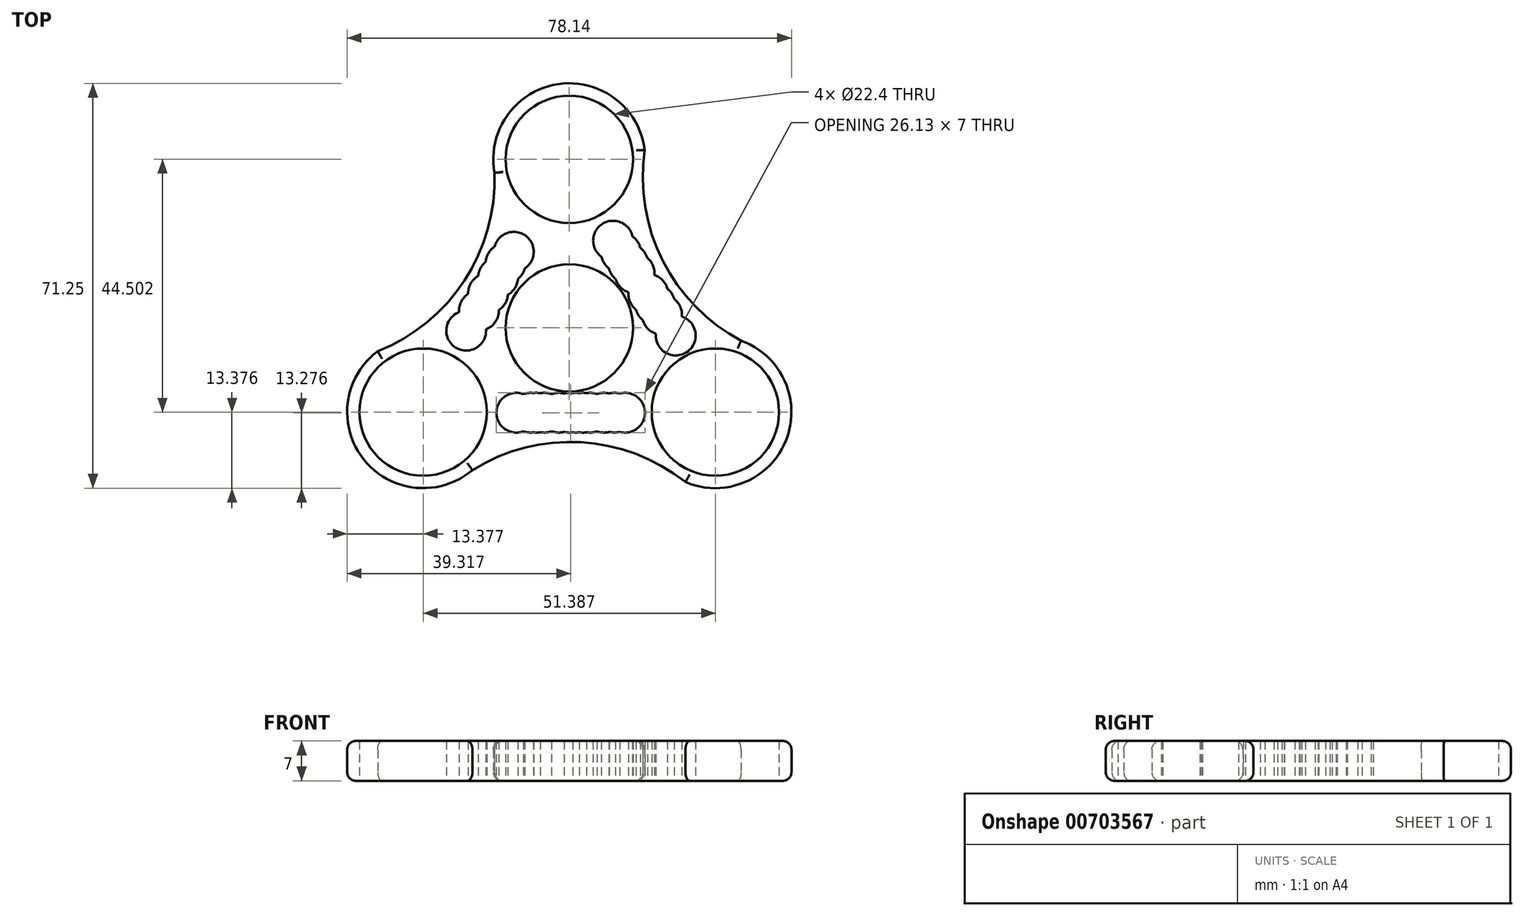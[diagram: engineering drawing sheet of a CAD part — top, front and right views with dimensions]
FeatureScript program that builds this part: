
annotation { "Feature Type Name" : "Feature", "Feature Type Description" : "" }
export const myFeature = defineFeature(function(context is Context, id is Id, definition is map)
    precondition{}
    {
        {
            var Q0;
            Q0=qCreatedBy(makeId("Top.planeOp"),FACE);
            var sketch = newSketch(context, id + "F0", { "sketchPlane" : qUnion([Q0])});
            skCircle(sketch, "E0", {"center": v(0, 0) * mm, "radius": 11.2 * mm});
            skCircle(sketch, "E1", {"center": v(0, 29.67) * mm, "radius": 11.2 * mm});
            skArc(sketch, "E2", {"start": v(12.93, 26.26) * mm, "mid": v(0.52, 43.03) * mm, "end": v(-13.16, 27.28) * mm});
            skArc(sketch, "E3.1.0", {"start": v(-29.21, -1.93) * mm, "mid": v(-37.53, -21.07) * mm, "end": v(-17.04, -25.03) * mm});
            skCircle(sketch, "E3.1.1", {"center": v(-25.7, -14.83) * mm, "radius": 11.2 * mm});
            skArc(sketch, "E3.2.0", {"start": v(16.28, -24.33) * mm, "mid": v(37, -21.97) * mm, "end": v(30.2, -2.24) * mm});
            skCircle(sketch, "E3.2.1", {"center": v(25.7, -14.83) * mm, "radius": 11.2 * mm});
            skArc(sketch, "E4", {"start": v(13.28, 31.24) * mm, "mid": v(16.43, 11.82) * mm, "end": v(30.2, -2.24) * mm});
            skArc(sketch, "E5.1.0", {"start": v(-33.7, -4.12) * mm, "mid": v(-18.45, 8.32) * mm, "end": v(-13.16, 27.28) * mm});
            skArc(sketch, "E5.2.0", {"start": v(20.42, -27.12) * mm, "mid": v(2.02, -20.14) * mm, "end": v(-17.04, -25.03) * mm});
            skSolve(sketch);
        }
        {
            var Q0;
            Q0=makeQuery(id+"F0.imprint","IMPRINT",FACE,{"disambiguationData":[TD([[makeQuery(id+"F0.imprint","IMPRINT",EDGE,{"derivedFrom":sQuery(id+"F0.wireOp",EDGE,"E0")}),-1.0]])]});
            extrude(context, id + "F1", {"entities" : qUnion([Q0]), "depth" : 7 * mm, "offsetDistance" : 25 * mm});
        }
        {
            var Q0;
            Q0=makeQuery(id+"F1.opExtrude","CAP_EDGE",EDGE,{"disambiguationData":[OSD([sQuery(id+"F0.wireOp",EDGE,"E5.1.0")])],"isStart":false});
            var Q1;
            Q1=makeQuery(id+"F1.opExtrude","CAP_EDGE",EDGE,{"disambiguationData":[OSD([sQuery(id+"F0.wireOp",EDGE,"E2")])],"isStart":false});
            var Q2;
            Q2=makeQuery(id+"F1.opExtrude","CAP_EDGE",EDGE,{"disambiguationData":[OSD([sQuery(id+"F0.wireOp",EDGE,"E4")])],"isStart":false});
            var Q3;
            Q3=makeQuery(id+"F1.opExtrude","CAP_EDGE",EDGE,{"disambiguationData":[OSD([sQuery(id+"F0.wireOp",EDGE,"E3.2.0")])],"isStart":false});
            var Q4;
            Q4=makeQuery(id+"F1.opExtrude","CAP_EDGE",EDGE,{"disambiguationData":[OSD([sQuery(id+"F0.wireOp",EDGE,"E5.2.0")])],"isStart":false});
            var Q5;
            Q5=makeQuery(id+"F1.opExtrude","CAP_EDGE",EDGE,{"disambiguationData":[OSD([sQuery(id+"F0.wireOp",EDGE,"E3.1.0")])],"isStart":false});
            fillet(context, id + "F2", {"entities" : qUnion([Q0, Q1, Q2, Q3, Q4, Q5]), "radius" : 1.5 * mm, "tangentPropagation" : true, "allowEdgeOverflow" : false});
        }
        {
            var Q0;
            Q0=makeQuery(id+"F1.opExtrude","CAP_EDGE",EDGE,{"disambiguationData":[OSD([sQuery(id+"F0.wireOp",EDGE,"E3.1.0")])],"isStart":true});
            var Q1;
            Q1=makeQuery(id+"F1.opExtrude","CAP_EDGE",EDGE,{"disambiguationData":[OSD([sQuery(id+"F0.wireOp",EDGE,"E5.2.0")])],"isStart":true});
            var Q2;
            Q2=makeQuery(id+"F1.opExtrude","CAP_EDGE",EDGE,{"disambiguationData":[OSD([sQuery(id+"F0.wireOp",EDGE,"E5.1.0")])],"isStart":true});
            var Q3;
            Q3=makeQuery(id+"F1.opExtrude","CAP_EDGE",EDGE,{"disambiguationData":[OSD([sQuery(id+"F0.wireOp",EDGE,"E2")])],"isStart":true});
            var Q4;
            Q4=makeQuery(id+"F1.opExtrude","CAP_EDGE",EDGE,{"disambiguationData":[OSD([sQuery(id+"F0.wireOp",EDGE,"E3.2.0")])],"isStart":true});
            var Q5;
            Q5=makeQuery(id+"F1.opExtrude","CAP_EDGE",EDGE,{"disambiguationData":[OSD([sQuery(id+"F0.wireOp",EDGE,"E4")])],"isStart":true});
            fillet(context, id + "F3", {"entities" : qUnion([Q0, Q1, Q2, Q3, Q4, Q5]), "radius" : 1.5 * mm, "tangentPropagation" : true, "allowEdgeOverflow" : false});
        }
        {
            var Q0;
            Q0=qCreatedBy(makeId("Top.planeOp"),FACE);
            var sketch = newSketch(context, id + "F4", { "sketchPlane" : qUnion([Q0])});
            skLineSegment(sketch, "E6", {"start": v(-14.58, 6.83) * mm, "end": v(-15.9, 5.37) * mm, "construction": true});
            skLineSegment(sketch, "E7", {"start": v(-15.9, 5.37) * mm, "end": v(-14.58, 6.83) * mm, "construction": true});
            skLineSegment(sketch, "E8", {"start": v(-15.9, 3.03) * mm, "end": v(-15.9, 0) * mm, "construction": true});
            skLineSegment(sketch, "E9", {"start": v(-15.9, 0) * mm, "end": v(-15.9, 3.03) * mm, "construction": true});
            skLineSegment(sketch, "E10", {"start": v(-12.53, 8.87) * mm, "end": v(-11.07, 10.92) * mm, "construction": true});
            skLineSegment(sketch, "E11", {"start": v(-11.07, 10.92) * mm, "end": v(-12.53, 8.87) * mm, "construction": true});
            skLineSegment(sketch, "E12", {"start": v(-9.76, 13.4) * mm, "end": v(-11.07, 10.92) * mm, "construction": true});
            skLineSegment(sketch, "E13", {"start": v(-9.76, 13.4) * mm, "end": v(-15.9, 5.37) * mm, "construction": true});
            skSolve(sketch);
        }
        {
            var Q0;
            Q0=sQuery(id+"F4.wireOp",VERTEX,"E12.start");
            var Q1;
            Q1=sQuery(id+"F4.wireOp",VERTEX,"E11.end");
            var Q2;
            Q2=sQuery(id+"F4.wireOp",VERTEX,"E8.start");
            var Q3;
            Q3=makeQuery(id+"F1.opExtrude","SWEPT_BODY",BODY,{"disambiguationData":[OSD([sQuery(id+"F0.wireOp",EDGE,"E0"),sQuery(id+"F0.wireOp",EDGE,"E1"),sQuery(id+"F0.wireOp",EDGE,"E2"),sQuery(id+"F0.wireOp",EDGE,"E3.1.0"),sQuery(id+"F0.wireOp",EDGE,"E3.1.1"),sQuery(id+"F0.wireOp",EDGE,"E3.2.0"),sQuery(id+"F0.wireOp",EDGE,"E3.2.1"),sQuery(id+"F0.wireOp",EDGE,"E4"),sQuery(id+"F0.wireOp",EDGE,"E5.1.0"),sQuery(id+"F0.wireOp",EDGE,"E5.2.0")])]});
            hole(context, id + "F5", {"style" : HoleStyle.SIMPLE, "endStyle" : HoleEndStyle.THROUGH, "oppositeDirection" : true, "holeDiameter" : 7 * mm, "majorDiameter" : 5 * mm, "isTappedThrough" : true, "tappedDepth" : 12 * mm, "tapClearance" : 3, "locations" : qUnion([Q0, Q1, Q2]), "scope" : qUnion([Q3])});
        }
        {
            var Q0;
            Q0=qCreatedBy(makeId("Top.planeOp"),FACE);
            var sketch = newSketch(context, id + "F6", { "sketchPlane" : qUnion([Q0])});
            skLineSegment(sketch, "E14", {"start": v(-9.61, -14.5) * mm, "end": v(9.08, -14.5) * mm, "construction": true});
            skLineSegment(sketch, "E15", {"start": v(9.08, -14.5) * mm, "end": v(0, -14.5) * mm, "construction": true});
            skLineSegment(sketch, "E16", {"start": v(0, -14.5) * mm, "end": v(4.54, -14.5) * mm, "construction": true});
            skLineSegment(sketch, "E17", {"start": v(4.54, -14.5) * mm, "end": v(-4.8, -14.5) * mm, "construction": true});
            skLineSegment(sketch, "E18", {"start": v(-4.8, -14.5) * mm, "end": v(6.9, -14.5) * mm, "construction": true});
            skLineSegment(sketch, "E19", {"start": v(6.9, -14.5) * mm, "end": v(-6.4, -14.5) * mm, "construction": true});
            skLineSegment(sketch, "E20", {"start": v(-6.4, -14.5) * mm, "end": v(2.27, -14.5) * mm, "construction": true});
            skLineSegment(sketch, "E21", {"start": v(9.08, 13.25) * mm, "end": v(18.72, -1.35) * mm, "construction": true});
            skLineSegment(sketch, "E22", {"start": v(18.72, -1.35) * mm, "end": v(13.9, 5.95) * mm, "construction": true});
            skLineSegment(sketch, "E23", {"start": v(13.9, 5.95) * mm, "end": v(16.31, 2.3) * mm, "construction": true});
            skLineSegment(sketch, "E24", {"start": v(16.31, 2.3) * mm, "end": v(11.5, 9.6) * mm, "construction": true});
            skLineSegment(sketch, "E25", {"start": v(11.5, 9.6) * mm, "end": v(10.38, 11.3) * mm, "construction": true});
            skLineSegment(sketch, "E26", {"start": v(10.38, 11.3) * mm, "end": v(7.7, 15.35) * mm, "construction": true});
            skLineSegment(sketch, "E27", {"start": v(7.7, 15.35) * mm, "end": v(15.1, 4.13) * mm, "construction": true});
            skLineSegment(sketch, "E28", {"start": v(15.1, 4.13) * mm, "end": v(16.31, 2.3) * mm, "construction": true});
            skSolve(sketch);
        }
        {
            var Q0;
            Q0=sQuery(id+"F6.wireOp",VERTEX,"E26.end");
            var Q1;
            Q1=sQuery(id+"F6.wireOp",VERTEX,"E21.start");
            var Q2;
            Q2=sQuery(id+"F6.wireOp",VERTEX,"E25.end");
            var Q3;
            Q3=sQuery(id+"F6.wireOp",VERTEX,"E25.start");
            var Q4;
            Q4=sQuery(id+"F6.wireOp",VERTEX,"E22.end");
            var Q5;
            Q5=sQuery(id+"F6.wireOp",VERTEX,"E27.end");
            var Q6;
            Q6=sQuery(id+"F6.wireOp",VERTEX,"E28.end");
            var Q7;
            Q7=sQuery(id+"F6.wireOp",VERTEX,"E21.end");
            var Q8;
            Q8=makeQuery(id+"F1.opExtrude","SWEPT_BODY",BODY,{"disambiguationData":[OSD([sQuery(id+"F0.wireOp",EDGE,"E0"),sQuery(id+"F0.wireOp",EDGE,"E1"),sQuery(id+"F0.wireOp",EDGE,"E2"),sQuery(id+"F0.wireOp",EDGE,"E3.1.0"),sQuery(id+"F0.wireOp",EDGE,"E3.1.1"),sQuery(id+"F0.wireOp",EDGE,"E3.2.0"),sQuery(id+"F0.wireOp",EDGE,"E3.2.1"),sQuery(id+"F0.wireOp",EDGE,"E4"),sQuery(id+"F0.wireOp",EDGE,"E5.1.0"),sQuery(id+"F0.wireOp",EDGE,"E5.2.0")])]});
            hole(context, id + "F7", {"style" : HoleStyle.SIMPLE, "endStyle" : HoleEndStyle.THROUGH, "oppositeDirection" : true, "holeDiameter" : 7 * mm, "majorDiameter" : 5 * mm, "isTappedThrough" : true, "tappedDepth" : 12 * mm, "tapClearance" : 3, "locations" : qUnion([Q0, Q1, Q2, Q3, Q4, Q5, Q6, Q7]), "scope" : qUnion([Q8])});
        }
        {
            var Q0;
            Q0=qCreatedBy(makeId("Top.planeOp"),FACE);
            var sketch = newSketch(context, id + "F8", { "sketchPlane" : qUnion([Q0])});
            skLineSegment(sketch, "E29", {"start": v(-11.22, 11.35) * mm, "end": v(-14.28, 6.1) * mm, "construction": true});
            skLineSegment(sketch, "E30", {"start": v(-14.28, 6.1) * mm, "end": v(-19, -2) * mm, "construction": true});
            skLineSegment(sketch, "E31", {"start": v(-19, -2) * mm, "end": v(-19, 0) * mm, "construction": true});
            skLineSegment(sketch, "E32", {"start": v(-19, 0) * mm, "end": v(-18.14, -0.5) * mm, "construction": true});
            skLineSegment(sketch, "E33", {"start": v(-18.14, -0.5) * mm, "end": v(-14.28, 6.1) * mm, "construction": true});
            skLineSegment(sketch, "E34", {"start": v(0, -14.93) * mm, "end": v(2.36, -14.93) * mm, "construction": true});
            skLineSegment(sketch, "E35", {"start": v(2.36, -14.93) * mm, "end": v(9.81, -14.93) * mm, "construction": true});
            skLineSegment(sketch, "E36", {"start": v(9.81, -14.93) * mm, "end": v(6.09, -14.93) * mm, "construction": true});
            skLineSegment(sketch, "E37", {"start": v(6.09, -14.93) * mm, "end": v(-4.35, -14.93) * mm, "construction": true});
            skPoint(sketch, "E37.endSnap0", {"position": v(1.18, -14.93) * mm});
            skLineSegment(sketch, "E38", {"start": v(-4.35, -14.93) * mm, "end": v(-1.87, -14.93) * mm, "construction": true});
            skLineSegment(sketch, "E39", {"start": v(-1.87, -14.93) * mm, "end": v(-6.84, -14.93) * mm, "construction": true});
            skLineSegment(sketch, "E40", {"start": v(-6.84, -14.93) * mm, "end": v(-9.32, -14.93) * mm, "construction": true});
            skLineSegment(sketch, "E41", {"start": v(-9.32, -14.93) * mm, "end": v(-11.22, -14.93) * mm, "construction": true});
            skLineSegment(sketch, "E42", {"start": v(-11.22, -14.93) * mm, "end": v(-6.84, -14.93) * mm, "construction": true});
            skLineSegment(sketch, "E43", {"start": v(-5.81, -14.93) * mm, "end": v(3.68, -14.93) * mm, "construction": true});
            skLineSegment(sketch, "E44", {"start": v(3.68, -14.93) * mm, "end": v(7.95, -14.93) * mm, "construction": true});
            skSolve(sketch);
        }
        {
            var Q0;
            Q0=sQuery(id+"F8.wireOp",VERTEX,"E41.start");
            var Q1;
            Q1=sQuery(id+"F8.wireOp",VERTEX,"E39.end");
            var Q2;
            Q2=sQuery(id+"F8.wireOp",VERTEX,"E37.end");
            var Q3;
            Q3=sQuery(id+"F8.wireOp",VERTEX,"E43.start");
            var Q4;
            Q4=sQuery(id+"F8.wireOp",VERTEX,"E38.end");
            var Q5;
            Q5=sQuery(id+"F8.wireOp",VERTEX,"E37.endSnap0");
            var Q6;
            Q6=sQuery(id+"F8.wireOp",VERTEX,"E34.start");
            var Q7;
            Q7=sQuery(id+"F8.wireOp",VERTEX,"E44.start");
            var Q8;
            Q8=sQuery(id+"F8.wireOp",VERTEX,"E34.end");
            var Q9;
            Q9=sQuery(id+"F8.wireOp",VERTEX,"E36.end");
            var Q10;
            Q10=sQuery(id+"F8.wireOp",VERTEX,"E44.end");
            var Q11;
            Q11=sQuery(id+"F8.wireOp",VERTEX,"E35.end");
            var Q12;
            Q12=sQuery(id+"F8.wireOp",VERTEX,"E30.start");
            var Q13;
            Q13=sQuery(id+"F8.wireOp",VERTEX,"E29.start");
            var Q14;
            Q14=sQuery(id+"F8.wireOp",VERTEX,"E32.end");
            var Q15;
            Q15=makeQuery(id+"F1.opExtrude","SWEPT_BODY",BODY,{"disambiguationData":[OSD([sQuery(id+"F0.wireOp",EDGE,"E0"),sQuery(id+"F0.wireOp",EDGE,"E1"),sQuery(id+"F0.wireOp",EDGE,"E2"),sQuery(id+"F0.wireOp",EDGE,"E3.1.0"),sQuery(id+"F0.wireOp",EDGE,"E3.1.1"),sQuery(id+"F0.wireOp",EDGE,"E3.2.0"),sQuery(id+"F0.wireOp",EDGE,"E3.2.1"),sQuery(id+"F0.wireOp",EDGE,"E4"),sQuery(id+"F0.wireOp",EDGE,"E5.1.0"),sQuery(id+"F0.wireOp",EDGE,"E5.2.0")])]});
            hole(context, id + "F9", {"style" : HoleStyle.SIMPLE, "endStyle" : HoleEndStyle.THROUGH, "oppositeDirection" : true, "holeDiameter" : 7 * mm, "majorDiameter" : 5 * mm, "isTappedThrough" : true, "tappedDepth" : 12 * mm, "tapClearance" : 3, "locations" : qUnion([Q0, Q1, Q2, Q3, Q4, Q5, Q6, Q7, Q8, Q9, Q10, Q11, Q12, Q13, Q14]), "scope" : qUnion([Q15])});
        }
    });
